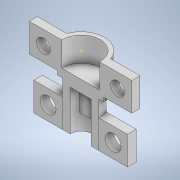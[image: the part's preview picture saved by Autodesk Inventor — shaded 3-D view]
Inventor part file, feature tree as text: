
AUTODESK INVENTOR PART (.ipt)
format: ipt  version: 2020.2 (Build 242310000, 310)  size: 294,912 bytes
history: native  units: in
note: dims shown in document units (in); Inventor stores cm internally (conversion verified against a paired STEP export)
features: sketch x16, extrude x11, plane x3, projected_geometry x3, hole x2
ambient origin geometry x8: Origin, YZ Plane, XZ Plane, XY Plane, X Axis, Y Axis, Z Axis, Center Point
bodies: Body1 (feature_tree)
feature tree (35):
  extrude  "Extrusion2"  Depth=0.3543in
  extrude  "Extrusion3"  Depth=0.0394in
  extrude  "Extrusion4"  Depth=0.0394in TaperAngle=0.0deg
  sketch  "Sketch11"  dims[d20=0.0394in d59=0.3681in]
  sketch  "Sketch12"  dims[d60=0.4476in d61=0.0787in d62=0.0in]
  extrude  "Extrusion11"  Depth=0.0394in
  extrude  "Extrusion12"  Depth=0.0787in TaperAngle=0.0deg
  sketch  "Sketch14"  dims[d63=0.315in d64=0.0in d72=0.0039in]
  sketch  "Sketch15"  dims[d73=0.2756in d74=0.2756in]
  plane  "Work Plane3"
  sketch  "Sketch17"  dims[d81=0.1378in d82=0.1378in]
  plane  "Work Plane2"
  extrude  "Extrusion17"  Depth=0.315in
  plane  "Work Plane1"
  extrude  "Extrusion18"  Depth=0.2756in
  extrude  "Extrusion20"  Depth=0.1378in
  hole  "Hole2"  [1 undecoded]
  sketch  "Sketch22"  dims[d99=0.0787in d100=0.0in d101=0.0787in d102=0.0in]
  sketch  "Sketch23"  dims[d104=3.0in d105=0.0in d106=0.2756in d107=0.0in]
  hole  "Hole3"  [1 undecoded]
  extrude  "Extrusion19"  Depth=0.154in
  extrude  "Extrusion21"  Depth=0.0787in TaperAngle=0.0deg
  extrude  "Extrusion22"  Depth=0.2756in TaperAngle=0.0deg
  sketch  "Sketch3"  dims[d10=0.3543in d11=0.2047in]
  sketch  "Sketch4"  dims[d12=0.1575in d13=0.0in d14=0.0394in]
  projected_geometry  "Projected Loop1"
  sketch  "Sketch5"  dims[d16=0.2362in d17=0.0in d18=0.0394in d19=0.0in]
  sketch  "Sketch19"  dims[d93=0.2756in d94=0.2756in]
  sketch  "Sketch20"  dims[d95=0.2756in d96=0.2756in]
  sketch  "Sketch21"  dims[d97=0.154in d98=0.154in]
  sketch  "Sketch24"  dims[d108=0.1339in d109=0.75in d110=0.248in d111=0.25in d112=90.0deg d113=1.0in d114=0.8108in]
  sketch  "Sketch25"  dims[d115=0.1339in d116=0.75in d117=0.248in d118=0.25in d119=90.0deg d120=1.0in d121=0.8108in]
  sketch  "Sketch26"  dims[d122=0.0787in d123=0.0in d124=1.0in d125=0.0in]
  projected_geometry  "Projected Loop3"
  projected_geometry  "Projected Loop4"
note: 2 required parameter values undecoded (feature->parameter linkage not recoverable at this tier; creation-order binding heuristic only, values carry confidence <= 0.55)
